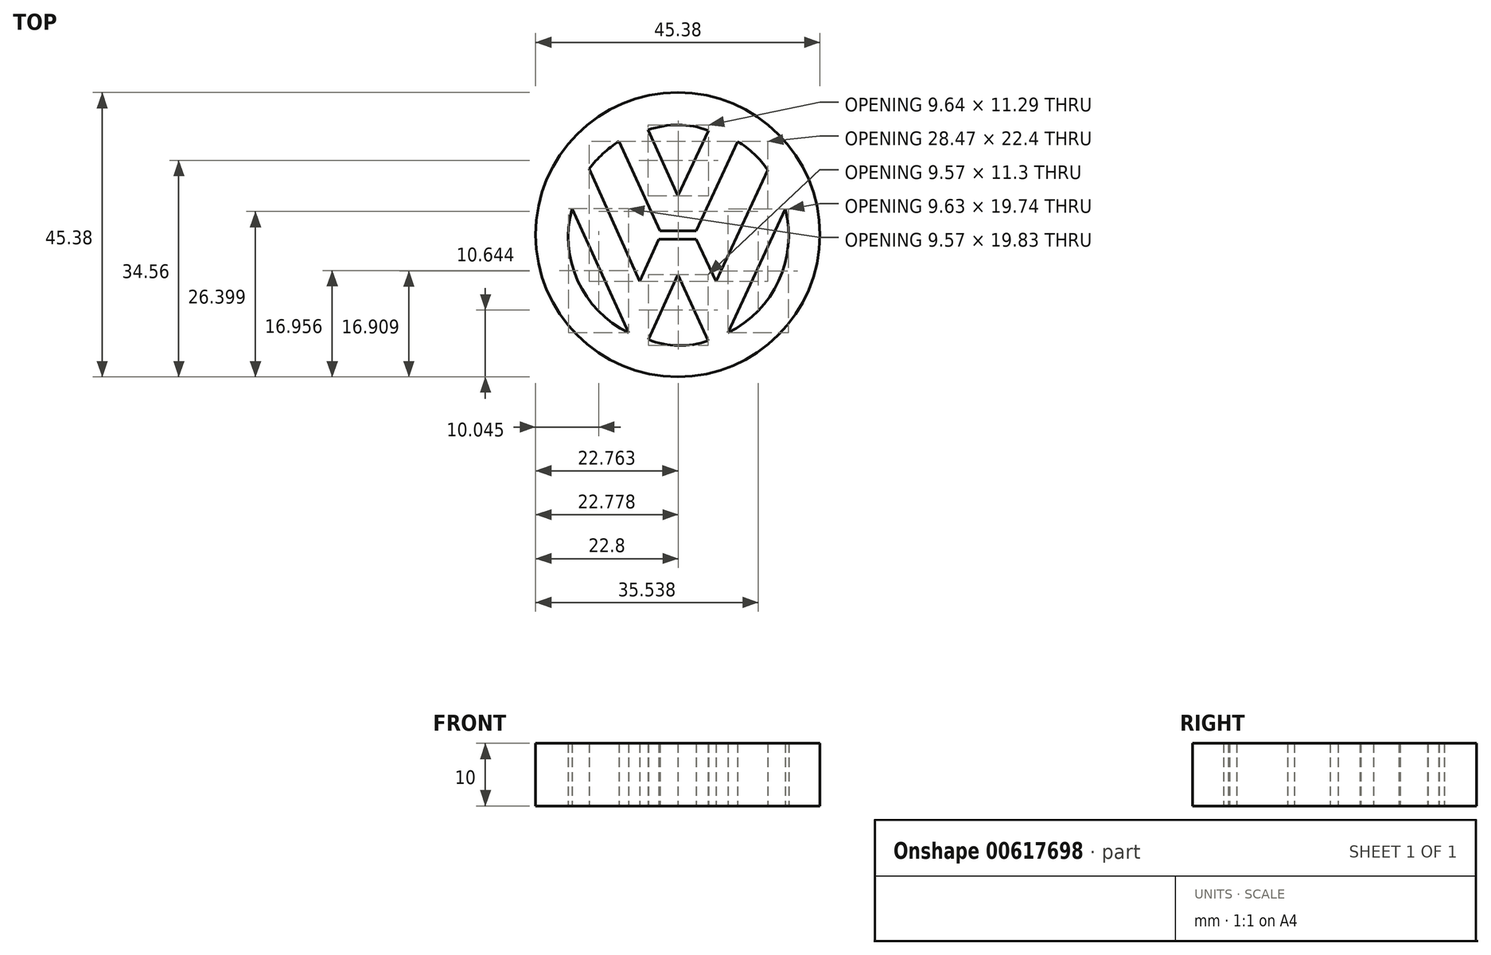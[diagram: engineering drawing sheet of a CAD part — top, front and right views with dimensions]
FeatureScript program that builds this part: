
annotation { "Feature Type Name" : "Feature", "Feature Type Description" : "" }
export const myFeature = defineFeature(function(context is Context, id is Id, definition is map)
    precondition{}
    {
        {
            var Q0;
            Q0=qCreatedBy(makeId("Top.planeOp"),FACE);
            var sketch = newSketch(context, id + "F0", { "sketchPlane" : qUnion([Q0])});
            skPoint(sketch, "E0.end.orphan", {"position": v(-27.95, 30.07) * mm});
            skLineSegment(sketch, "E1", {"start": v(0, 6.22) * mm, "end": v(4.9, 16.62) * mm});
            skLineSegment(sketch, "E2", {"start": v(0, 6.22) * mm, "end": v(-4.73, 16.7) * mm});
            skArc(sketch, "E3", {"start": v(4.9, 16.62) * mm, "mid": v(0.1, 17.52) * mm, "end": v(-4.73, 16.7) * mm});
            skLineSegment(sketch, "E4", {"start": v(-2.83, 0.58) * mm, "end": v(2.96, 0.58) * mm});
            skLineSegment(sketch, "E5", {"start": v(2.96, 0.58) * mm, "end": v(9.55, 14.86) * mm});
            skLineSegment(sketch, "E6", {"start": v(-2.83, 0.58) * mm, "end": v(-9.38, 14.9) * mm});
            skLineSegment(sketch, "E7", {"start": v(-14.12, 10.5) * mm, "end": v(-6.1, -7.49) * mm});
            skLineSegment(sketch, "E8", {"start": v(-6.1, -7.49) * mm, "end": v(-3.02, -0.7) * mm});
            skLineSegment(sketch, "E9", {"start": v(-3.02, -0.7) * mm, "end": v(2.96, -0.7) * mm});
            skLineSegment(sketch, "E10", {"start": v(2.96, -0.7) * mm, "end": v(6.09, -7.49) * mm});
            skLineSegment(sketch, "E11", {"start": v(6.09, -7.49) * mm, "end": v(14.35, 10.3) * mm});
            skArc(sketch, "E12", {"start": v(-9.38, 14.9) * mm, "mid": v(-11.95, 12.92) * mm, "end": v(-14.12, 10.5) * mm});
            skArc(sketch, "E13", {"start": v(14.35, 10.3) * mm, "mid": v(12.21, 12.86) * mm, "end": v(9.55, 14.86) * mm});
            skLineSegment(sketch, "E14", {"start": v(0, -6.4) * mm, "end": v(-4.7, -16.76) * mm});
            skLineSegment(sketch, "E15", {"start": v(0, -6.4) * mm, "end": v(4.86, -16.93) * mm});
            skArc(sketch, "E16", {"start": v(-4.7, -16.76) * mm, "mid": v(0.06, -17.7) * mm, "end": v(4.86, -16.93) * mm});
            skLineSegment(sketch, "E17", {"start": v(-16.88, 4.18) * mm, "end": v(-7.86, -15.65) * mm});
            skArc(sketch, "E18", {"start": v(-16.88, 4.18) * mm, "mid": v(-15.96, -7.36) * mm, "end": v(-7.86, -15.65) * mm});
            skLineSegment(sketch, "E19", {"start": v(8.03, -15.65) * mm, "end": v(17.2, 4.09) * mm});
            skArc(sketch, "E20", {"start": v(8.03, -15.65) * mm, "mid": v(16.1, -7.4) * mm, "end": v(17.2, 4.09) * mm});
            skCircle(sketch, "E21", {"center": v(0, 0) * mm, "radius": 22.69 * mm});
            skSolve(sketch);
        }
        {
            var Q0;
            Q0 = qSketchRegion(id + "F0", true);
            extrude(context, id + "F1", {"entities" : qUnion([Q0]), "depth" : 10 * mm, "offsetDistance" : 25 * mm});
        }
    });
